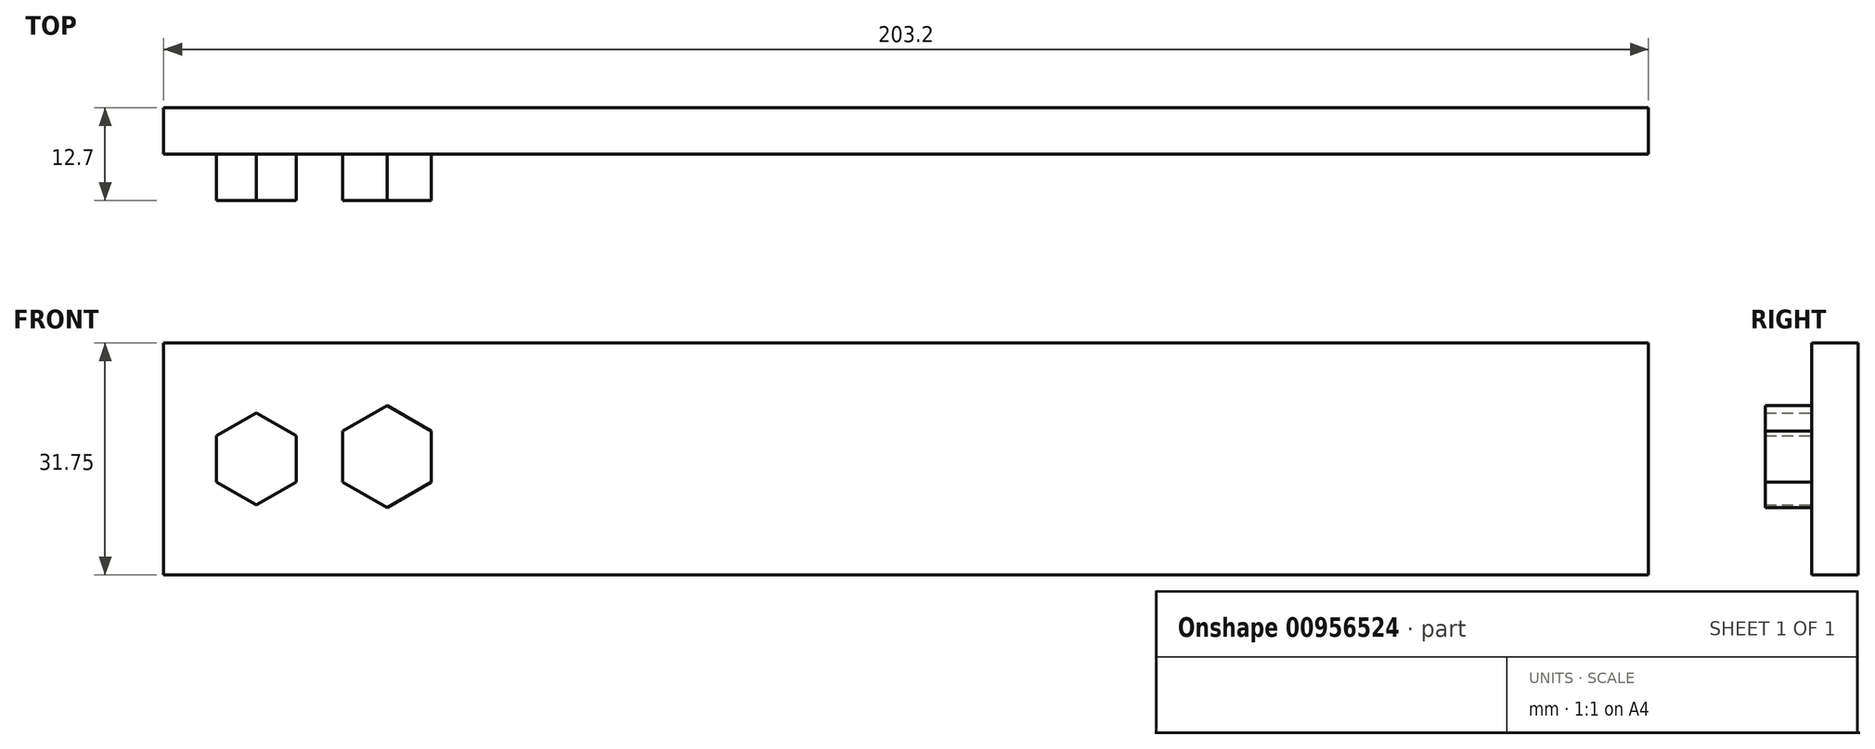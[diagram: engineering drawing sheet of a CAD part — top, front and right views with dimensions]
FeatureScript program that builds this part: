
annotation { "Feature Type Name" : "Feature", "Feature Type Description" : "" }
export const myFeature = defineFeature(function(context is Context, id is Id, definition is map)
    precondition{}
    {
        {
            var Q0;
            Q0=qCreatedBy(makeId("Front.planeOp"),FACE);
            var sketch = newSketch(context, id + "F0", { "sketchPlane" : qUnion([Q0])});
            skLineSegment(sketch, "E0.bottom", {"start": v(0, 0) * mm, "end": v(203.2, 0) * mm});
            skLineSegment(sketch, "E0.top", {"start": v(0, 31.75) * mm, "end": v(203.2, 31.75) * mm});
            skLineSegment(sketch, "E0.left", {"start": v(0, 0) * mm, "end": v(0, 31.75) * mm});
            skLineSegment(sketch, "E0.right", {"start": v(203.2, 0) * mm, "end": v(203.2, 31.75) * mm});
            skSolve(sketch);
        }
        {
            var Q0;
            Q0 = qSketchRegion(id + "F0", true);
            extrude(context, id + "F1", {"entities" : qUnion([Q0]), "depth" : 6.35 * mm, "offsetDistance" : 25.4 * mm});
        }
        {
            var Q0;
            Q0=makeQuery(id+"F1.opExtrude","CAP_FACE",FACE,{"disambiguationData":[OSD([sQuery(id+"F0.wireOp",EDGE,"E0.bottom"),sQuery(id+"F0.wireOp",EDGE,"E0.top"),sQuery(id+"F0.wireOp",EDGE,"E0.left"),sQuery(id+"F0.wireOp",EDGE,"E0.right")])],"isStart":false});
            var sketch = newSketch(context, id + "F2", { "sketchPlane" : qUnion([Q0])});
            skCircle(sketch, "E1.cCircle", {"center": v(12.7, 15.88) * mm, "radius": 5.46 * mm, "construction": true});
            skLineSegment(sketch, "E1.0", {"start": v(18.16, 19.03) * mm, "end": v(18.16, 12.72) * mm});
            skLineSegment(sketch, "E1.1", {"start": v(18.16, 12.72) * mm, "end": v(12.7, 9.57) * mm});
            skLineSegment(sketch, "E1.2", {"start": v(12.7, 9.57) * mm, "end": v(7.24, 12.72) * mm});
            skLineSegment(sketch, "E1.3", {"start": v(7.24, 12.72) * mm, "end": v(7.24, 19.03) * mm});
            skLineSegment(sketch, "E1.4", {"start": v(7.24, 19.03) * mm, "end": v(12.7, 22.18) * mm});
            skLineSegment(sketch, "E1.5", {"start": v(12.7, 22.18) * mm, "end": v(18.16, 19.03) * mm});
            skPoint(sketch, "E1.0.midPoint", {"position": v(18.16, 15.88) * mm});
            skSolve(sketch);
        }
        {
            var Q0;
            Q0=makeQuery(id+"F2.imprint","IMPRINT",FACE,{"disambiguationData":[TD([[makeQuery(id+"F2.imprint","IMPRINT",EDGE,{"derivedFrom":sQuery(id+"F2.wireOp",EDGE,"E1.0")}),-1.0]])]});
            extrude(context, id + "F3", {"entities" : qUnion([Q0]), "operationType" : NewBodyOperationType.ADD, "depth" : 6.35 * mm, "offsetDistance" : 25.4 * mm});
        }
        {
            var Q0;
            Q0=makeQuery(id+"F1.opExtrude","CAP_FACE",FACE,{"disambiguationData":[OSD([sQuery(id+"F0.wireOp",EDGE,"E0.bottom"),sQuery(id+"F0.wireOp",EDGE,"E0.top"),sQuery(id+"F0.wireOp",EDGE,"E0.left"),sQuery(id+"F0.wireOp",EDGE,"E0.right")])],"isStart":false});
            var sketch = newSketch(context, id + "F4", { "sketchPlane" : qUnion([Q0])});
            skCircle(sketch, "E2.cCircle", {"center": v(30.56, 16.21) * mm, "radius": 6.05 * mm, "construction": true});
            skLineSegment(sketch, "E2.0", {"start": v(36.6, 19.7) * mm, "end": v(36.6, 12.72) * mm});
            skLineSegment(sketch, "E2.1", {"start": v(36.6, 12.72) * mm, "end": v(30.56, 9.23) * mm});
            skLineSegment(sketch, "E2.2", {"start": v(30.56, 9.23) * mm, "end": v(24.51, 12.72) * mm});
            skLineSegment(sketch, "E2.3", {"start": v(24.51, 12.72) * mm, "end": v(24.51, 19.7) * mm});
            skLineSegment(sketch, "E2.4", {"start": v(24.51, 19.7) * mm, "end": v(30.56, 23.2) * mm});
            skLineSegment(sketch, "E2.5", {"start": v(30.56, 23.2) * mm, "end": v(36.6, 19.7) * mm});
            skPoint(sketch, "E2.0.midPoint", {"position": v(36.6, 16.21) * mm});
            skSolve(sketch);
        }
        {
            var Q0;
            Q0 = qSketchRegion(id + "F4", true);
            extrude(context, id + "F5", {"entities" : qUnion([Q0]), "operationType" : NewBodyOperationType.ADD, "depth" : 6.35 * mm, "offsetDistance" : 25.4 * mm});
        }
    });
